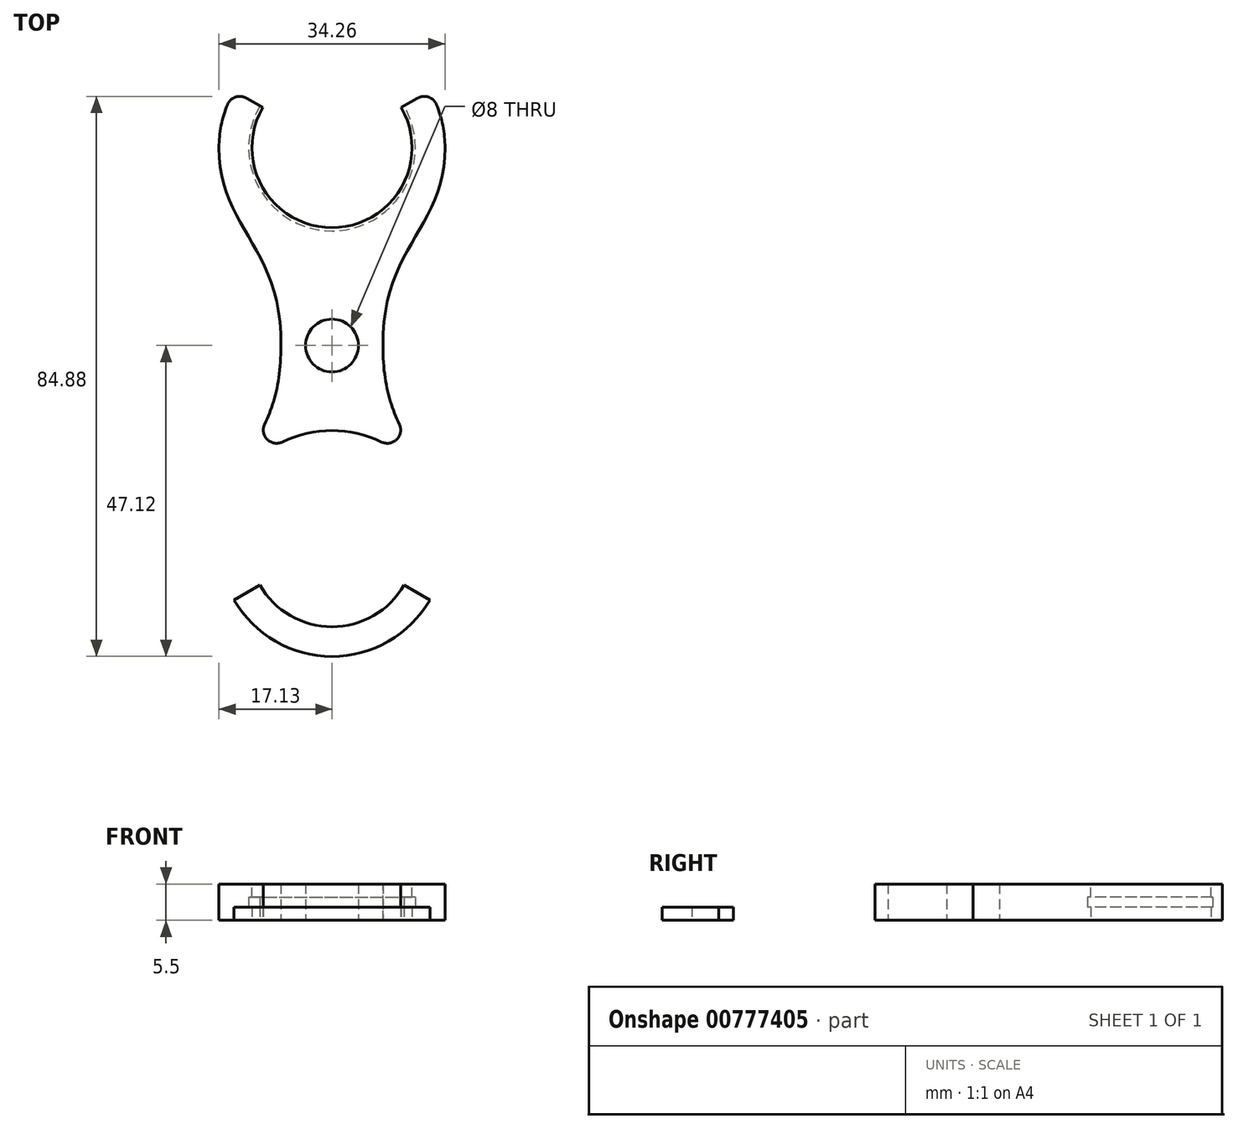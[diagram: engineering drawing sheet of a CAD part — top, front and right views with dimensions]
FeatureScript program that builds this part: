
annotation { "Feature Type Name" : "Feature", "Feature Type Description" : "" }
export const myFeature = defineFeature(function(context is Context, id is Id, definition is map)
    precondition{}
    {
        {
            var Q0;
            Q0=qCreatedBy(makeId("Top.planeOp"),FACE);
            var sketch = newSketch(context, id + "F0", { "sketchPlane" : qUnion([Q0])});
            skCircle(sketch, "E0", {"center": v(0, 30) * mm, "radius": 12.12 * mm});
            skCircle(sketch, "E1", {"center": v(0, 30) * mm, "radius": 17.12 * mm});
            skCircle(sketch, "E2", {"center": v(0, 0) * mm, "radius": 4 * mm});
            skFitSpline(sketch, "E3", {"points": [v(-17.12, 30) * mm, v(-7.77, 0) * mm], "startDerivative": vector(-0.29, -35.92) * mm, "endDerivative": vector(-1.01, -44.07) * mm});
            skFitSpline(sketch, "E4.MirrorCS", {"points": [v(17.12, 30) * mm, v(7.77, 0) * mm], "startDerivative": vector(0.29, -35.92) * mm, "endDerivative": vector(1.01, -44.07) * mm});
            skFitSpline(sketch, "E5.MirrorCS", {"points": [v(-17.12, -30) * mm, v(-7.77, 0) * mm], "startDerivative": vector(-0.29, 35.92) * mm, "endDerivative": vector(-1.01, 44.07) * mm});
            skFitSpline(sketch, "E6.MirrorCS", {"points": [v(17.12, -30) * mm, v(7.77, 0) * mm], "startDerivative": vector(0.29, 35.92) * mm, "endDerivative": vector(1.01, 44.07) * mm});
            skCircle(sketch, "E7.MirrorC", {"center": v(0, -30) * mm, "radius": 17.12 * mm});
            skCircle(sketch, "E8.MirrorC", {"center": v(0, -30) * mm, "radius": 12.12 * mm});
            skLineSegment(sketch, "E9", {"start": v(0, 30) * mm, "end": v(-10.5, 36.06) * mm});
            skLineSegment(sketch, "E10.MirrorCS", {"start": v(0, 30) * mm, "end": v(10.5, 36.06) * mm});
            skLineSegment(sketch, "E11.MirrorCS", {"start": v(0, -30) * mm, "end": v(-10.5, -36.06) * mm});
            skLineSegment(sketch, "E12.MirrorCS", {"start": v(0, -30) * mm, "end": v(10.5, -36.06) * mm});
            skLineSegment(sketch, "E13", {"start": v(-14.83, 38.56) * mm, "end": v(-29.72, 47.16) * mm});
            skLineSegment(sketch, "E14", {"start": v(-10.5, 36.06) * mm, "end": v(-14.83, 38.56) * mm});
            skLineSegment(sketch, "E15", {"start": v(10.5, 36.06) * mm, "end": v(14.83, 38.56) * mm});
            skLineSegment(sketch, "E16", {"start": v(14.83, 38.56) * mm, "end": v(29.72, 47.16) * mm});
            skLineSegment(sketch, "E17", {"start": v(-14.83, -38.56) * mm, "end": v(-29.72, -47.16) * mm});
            skLineSegment(sketch, "E18", {"start": v(-10.5, -36.06) * mm, "end": v(-14.83, -38.56) * mm});
            skLineSegment(sketch, "E19", {"start": v(10.5, -36.06) * mm, "end": v(29.72, -47.16) * mm});
            skCircle(sketch, "E20", {"center": v(0, 30) * mm, "radius": 12.62 * mm});
            skCircle(sketch, "E21.MirrorC", {"center": v(0, -30) * mm, "radius": 12.62 * mm});
            skSolve(sketch);
        }
        {
            var Q0;
            Q0=makeQuery(id+"F0.imprint","IMPRINT",FACE,{"disambiguationData":[TD([[makeQuery(id+"F0.imprint","IMPRINT",EDGE,{"derivedFrom":sQuery(id+"F0.wireOp",EDGE,"E2")}),-1.0]])]});
            var Q1;
            {var subQ0=sQuery(id+"F0.wireOp",EDGE,"E1");var subQ2=makeQuery(id+"F0.imprint","INTERSECT",VERTEX,{"derivedFrom":[subQ0,sQuery(id+"F0.wireOp",EDGE,"E4.MirrorCS")]});Q1=makeQuery(id+"F0.imprint","IMPRINT",FACE,{"disambiguationData":[TD([[makeQuery(id+"F0.imprint","IMPRINT",EDGE,{"disambiguationData":[TD([[subQ2,-1.0]])],"derivedFrom":subQ0}),1.0]])]});}
            var Q2;
            {var subQ0=sQuery(id+"F0.wireOp",EDGE,"E7.MirrorC");var subQ2=makeQuery(id+"F0.imprint","INTERSECT",VERTEX,{"derivedFrom":[sQuery(id+"F0.wireOp",EDGE,"E6.MirrorCS"),subQ0]});Q2=makeQuery(id+"F0.imprint","IMPRINT",FACE,{"disambiguationData":[TD([[makeQuery(id+"F0.imprint","IMPRINT",EDGE,{"disambiguationData":[TD([[subQ2,-1.0]])],"derivedFrom":subQ0}),-1.0]])]});}
            extrude(context, id + "F1", {"entities" : qUnion([Q0, Q1, Q2]), "depth" : 5.5 * mm, "offsetDistance" : 25 * mm});
        }
        {
            var Q0;
            Q0=makeQuery(id+"F1.opExtrude","SWEPT_EDGE",EDGE,{"disambiguationData":[OSD([sQuery(id+"F0.wireOp",EDGE,"E7.MirrorC"),sQuery(id+"F0.wireOp",EDGE,"E18")])]});
            var Q1;
            Q1=makeQuery(id+"F1.opExtrude","SWEPT_EDGE",EDGE,{"disambiguationData":[OSD([sQuery(id+"F0.wireOp",EDGE,"E7.MirrorC"),sQuery(id+"F0.wireOp",EDGE,"E19")])]});
            var Q2;
            Q2=makeQuery(id+"F1.opExtrude","SWEPT_EDGE",EDGE,{"disambiguationData":[OSD([sQuery(id+"F0.wireOp",EDGE,"E1"),sQuery(id+"F0.wireOp",EDGE,"E14")])]});
            var Q3;
            Q3=makeQuery(id+"F1.opExtrude","SWEPT_EDGE",EDGE,{"disambiguationData":[OSD([sQuery(id+"F0.wireOp",EDGE,"E1"),sQuery(id+"F0.wireOp",EDGE,"E15")])]});
            fillet(context, id + "F2", {"entities" : qUnion([Q0, Q1, Q2, Q3]), "radius" : 2 * mm, "tangentPropagation" : true, "allowEdgeOverflow" : false});
        }
        {
            var Q0;
            {var subQ0=sQuery(id+"F0.wireOp",EDGE,"E14");var subQ5=sQuery(id+"F0.wireOp",EDGE,"E20");var subQ6=makeQuery(id+"F0.imprint","INTERSECT",VERTEX,{"derivedFrom":[subQ0,subQ5]});Q0=makeQuery(id+"F0.imprint","IMPRINT",FACE,{"disambiguationData":[TD([[makeQuery(id+"F0.imprint","IMPRINT",EDGE,{"disambiguationData":[TD([[subQ6,-1.0]])],"derivedFrom":subQ5}),1.0]])]});}
            var Q1;
            {var subQ0=sQuery(id+"F0.wireOp",EDGE,"E18");var subQ5=sQuery(id+"F0.wireOp",EDGE,"E21.MirrorC");var subQ6=makeQuery(id+"F0.imprint","INTERSECT",VERTEX,{"derivedFrom":[subQ0,subQ5]});Q1=makeQuery(id+"F0.imprint","IMPRINT",FACE,{"disambiguationData":[TD([[makeQuery(id+"F0.imprint","IMPRINT",EDGE,{"disambiguationData":[TD([[subQ6,-1.0]])],"derivedFrom":subQ5}),-1.0]])]});}
            extrude(context, id + "F3", {"entities" : qUnion([Q0, Q1]), "operationType" : NewBodyOperationType.ADD, "depth" : 2 * mm, "offsetDistance" : 25 * mm});
        }
        {
            var Q0;
            Q0=makeQuery(id+"F1.opExtrude","CAP_FACE",FACE,{"disambiguationData":[OSD([sQuery(id+"F0.wireOp",EDGE,"E0"),sQuery(id+"F0.wireOp",EDGE,"E1"),sQuery(id+"F0.wireOp",EDGE,"E2"),sQuery(id+"F0.wireOp",EDGE,"E3"),sQuery(id+"F0.wireOp",EDGE,"E4.MirrorCS"),sQuery(id+"F0.wireOp",EDGE,"E5.MirrorCS"),sQuery(id+"F0.wireOp",EDGE,"E6.MirrorCS"),sQuery(id+"F0.wireOp",EDGE,"E7.MirrorC"),sQuery(id+"F0.wireOp",EDGE,"E8.MirrorC"),sQuery(id+"F0.wireOp",EDGE,"E14"),sQuery(id+"F0.wireOp",EDGE,"E15"),sQuery(id+"F0.wireOp",EDGE,"E18"),sQuery(id+"F0.wireOp",EDGE,"E19")])],"isStart":false});
            var sketch = newSketch(context, id + "F4", { "sketchPlane" : qUnion([Q0])});
            skLineSegment(sketch, "E22.0", {"start": v(-10.5, 36.06) * mm, "end": v(-10.93, 36.31) * mm});
            skCircle(sketch, "E23.0", {"center": v(0, 30) * mm, "radius": 12.12 * mm});
            skLineSegment(sketch, "E24.0", {"start": v(10.5, 36.06) * mm, "end": v(14.83, 38.56) * mm});
            skCircle(sketch, "E25.0", {"center": v(0, -30) * mm, "radius": 12.12 * mm});
            skLineSegment(sketch, "E26.0", {"start": v(-10.5, -36.06) * mm, "end": v(-14.83, -38.56) * mm});
            skLineSegment(sketch, "E27.0", {"start": v(10.5, -36.06) * mm, "end": v(29.72, -47.16) * mm});
            skLineSegment(sketch, "E28", {"start": v(-10.93, 36.31) * mm, "end": v(-14.83, 38.56) * mm});
            skArc(sketch, "E29", {"start": v(10.93, 36.31) * mm, "mid": v(0, 42.62) * mm, "end": v(-10.93, 36.31) * mm});
            skArc(sketch, "E30", {"start": v(-10.93, 36.31) * mm, "mid": v(0, 17.37) * mm, "end": v(10.93, 36.31) * mm});
            skArc(sketch, "E31", {"start": v(-10.93, -36.31) * mm, "mid": v(0, -17.37) * mm, "end": v(10.93, -36.31) * mm});
            skArc(sketch, "E32", {"start": v(10.93, -36.31) * mm, "mid": v(0, -42.62) * mm, "end": v(-10.93, -36.31) * mm});
            skSolve(sketch);
        }
        {
            var Q0;
            {var subQ0=sQuery(id+"F4.wireOp",EDGE,"E22.0");Q0=makeQuery(id+"F4.imprint","IMPRINT",FACE,{"disambiguationData":[TD([[makeQuery(id+"F4.imprint","IMPRINT",EDGE,{"derivedFrom":subQ0}),1.0]])]});}
            var Q1;
            {var subQ6=sQuery(id+"F4.wireOp",EDGE,"E31");Q1=makeQuery(id+"F4.imprint","IMPRINT",FACE,{"disambiguationData":[TD([[makeQuery(id+"F4.imprint","IMPRINT",EDGE,{"derivedFrom":subQ6}),-1.0]])]});}
            extrude(context, id + "F5", {"entities" : qUnion([Q0, Q1]), "operationType" : NewBodyOperationType.ADD, "oppositeDirection" : true, "depth" : 2 * mm, "offsetDistance" : 25 * mm});
        }
    });
